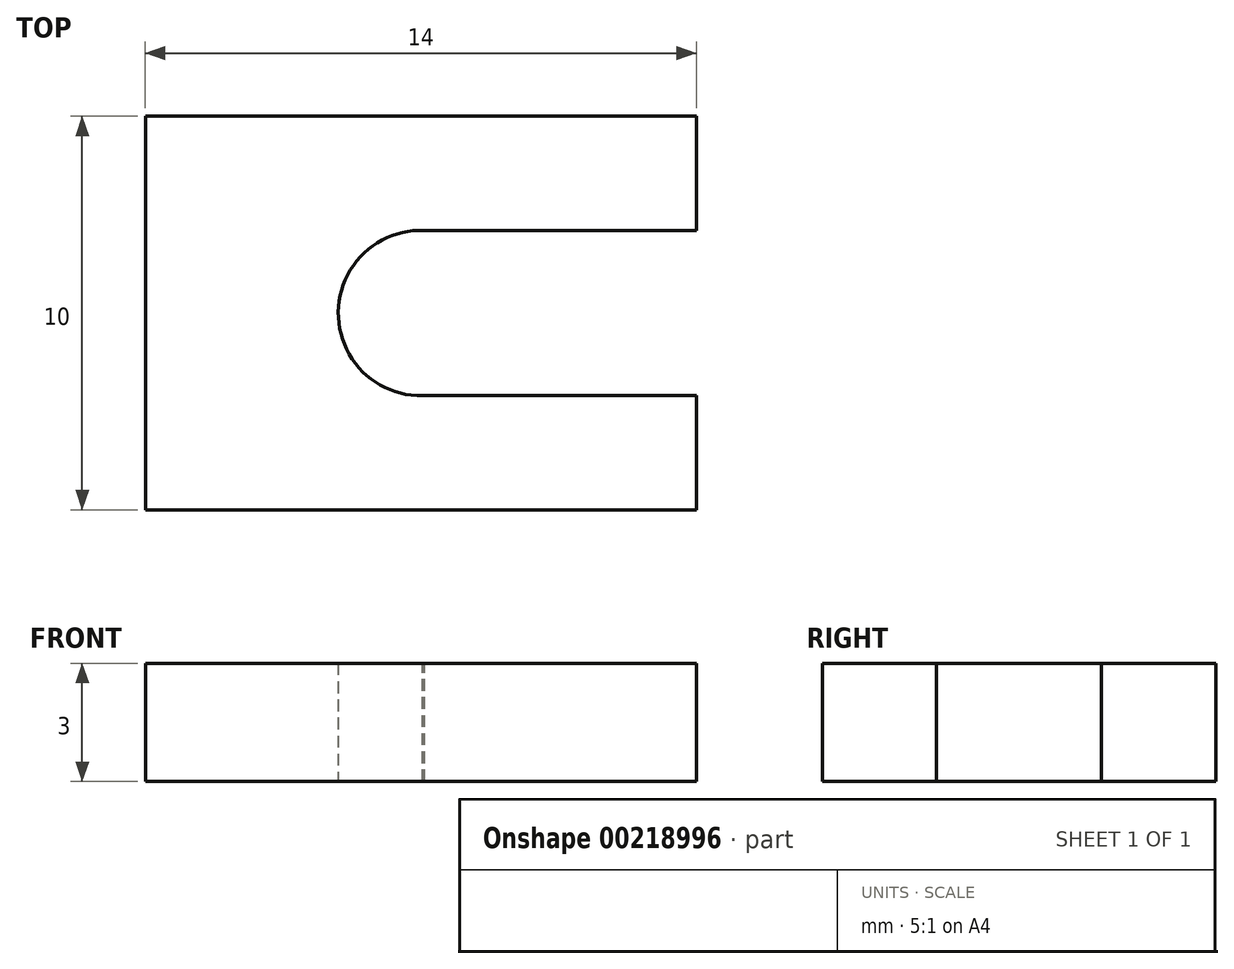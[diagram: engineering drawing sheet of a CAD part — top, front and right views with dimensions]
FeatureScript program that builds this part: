
annotation { "Feature Type Name" : "Feature", "Feature Type Description" : "" }
export const myFeature = defineFeature(function(context is Context, id is Id, definition is map)
    precondition{}
    {
        {
            var Q0;
            Q0=qCreatedBy(makeId("Top.planeOp"),FACE);
            var sketch = newSketch(context, id + "F0", { "sketchPlane" : qUnion([Q0])});
            skLineSegment(sketch, "E0.bottom", {"start": v(-24.95, 9.86) * mm, "end": v(-10.95, 9.86) * mm});
            skLineSegment(sketch, "E0.top", {"start": v(-24.95, -0.14) * mm, "end": v(-10.95, -0.14) * mm});
            skLineSegment(sketch, "E0.left", {"start": v(-24.95, 9.86) * mm, "end": v(-24.95, -0.14) * mm});
            skLineSegment(sketch, "E0.right", {"start": v(-10.95, 9.86) * mm, "end": v(-10.95, -0.14) * mm});
            skCircle(sketch, "E1", {"center": v(-17.95, 4.86) * mm, "radius": 2.1 * mm});
            skSolve(sketch);
        }
        {
            var Q0;
            Q0=makeQuery(id+"F0.imprint","IMPRINT",FACE,{"disambiguationData":[TD([[makeQuery(id+"F0.imprint","IMPRINT",EDGE,{"derivedFrom":sQuery(id+"F0.wireOp",EDGE,"E0.bottom")}),-1.0]])]});
            extrude(context, id + "F1", {"entities" : qUnion([Q0]), "depth" : 3 * mm});
        }
        {
            var Q0;
            Q0=makeQuery(id+"F1.opExtrude","CAP_FACE",FACE,{"disambiguationData":[OSD([sQuery(id+"F0.wireOp",EDGE,"E0.bottom"),sQuery(id+"F0.wireOp",EDGE,"E0.top"),sQuery(id+"F0.wireOp",EDGE,"E0.left"),sQuery(id+"F0.wireOp",EDGE,"E0.right"),sQuery(id+"F0.wireOp",EDGE,"E1")])],"isStart":false});
            var sketch = newSketch(context, id + "F2", { "sketchPlane" : qUnion([Q0])});
            skLineSegment(sketch, "E2", {"start": v(-17.86, 6.96) * mm, "end": v(-10.95, 6.96) * mm});
            skLineSegment(sketch, "E3", {"start": v(-17.9, 2.76) * mm, "end": v(-10.95, 2.76) * mm});
            skLineSegment(sketch, "E4", {"start": v(-10.95, 2.76) * mm, "end": v(-10.95, 6.96) * mm});
            skSolve(sketch);
        }
        {
            var Q0;
            Q0 = qSketchRegion(id + "F2", true);
            var Q1;
            {var subQ0=sQuery(id+"F2.wireOp",EDGE,"E2");Q1=makeQuery(id+"F2.imprint","IMPRINT",FACE,{"disambiguationData":[TD([[makeQuery(id+"F2.imprint","IMPRINT",EDGE,{"derivedFrom":subQ0}),-1.0]])]});}
            extrude(context, id + "F3", {"entities" : qUnion([Q0, Q1]), "operationType" : NewBodyOperationType.REMOVE, "oppositeDirection" : true, "depth" : 25 * mm});
        }
    });
